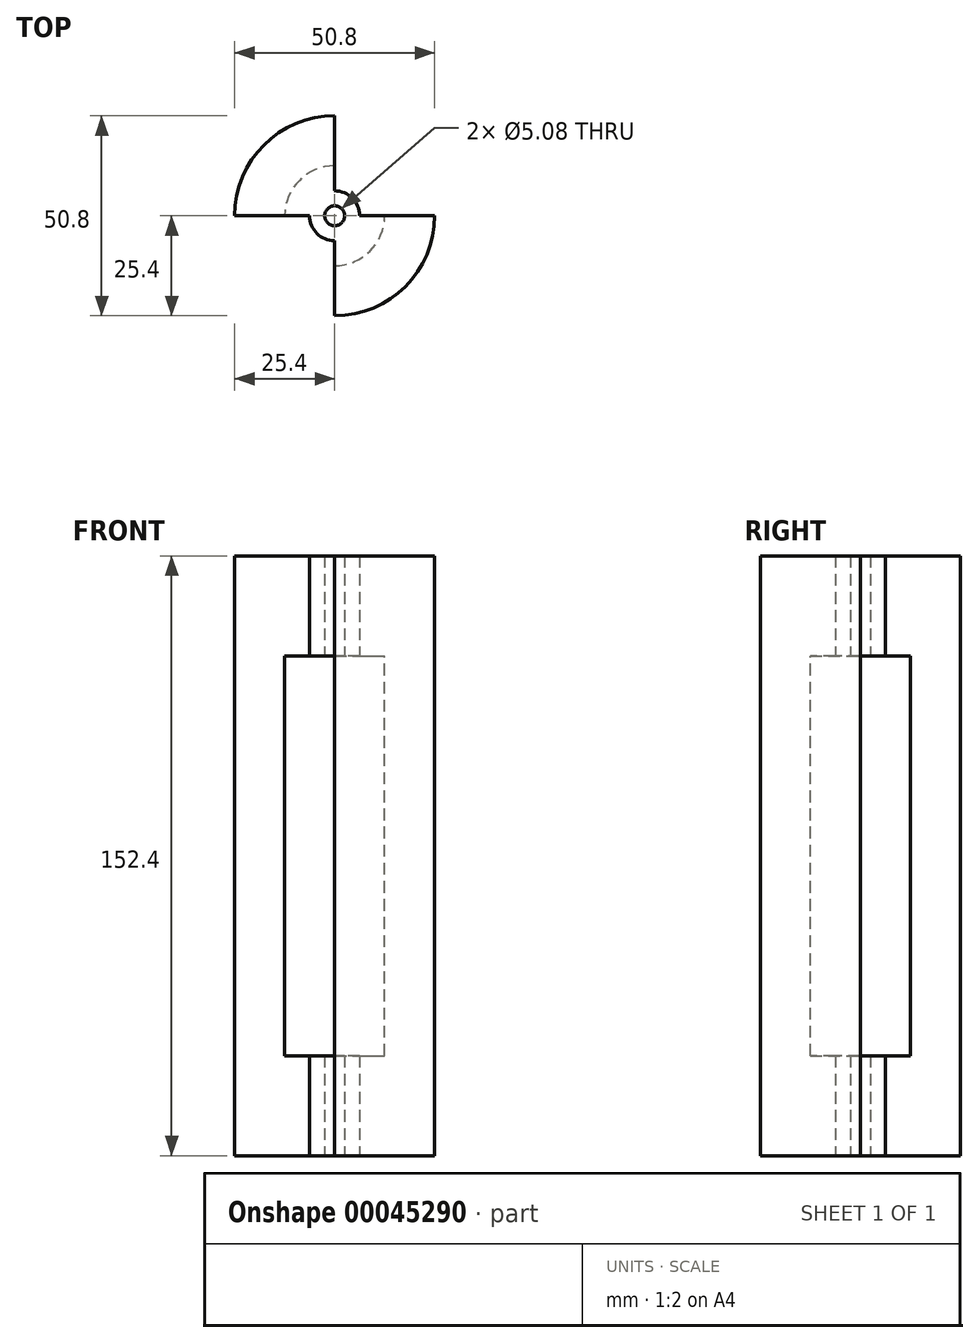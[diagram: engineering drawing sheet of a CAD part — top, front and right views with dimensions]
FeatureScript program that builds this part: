
annotation { "Feature Type Name" : "Feature", "Feature Type Description" : "" }
export const myFeature = defineFeature(function(context is Context, id is Id, definition is map)
    precondition{}
    {
        {
            var Q0;
            Q0=qCreatedBy(makeId("Top.planeOp"),FACE);
            var sketch = newSketch(context, id + "F0", { "sketchPlane" : qUnion([Q0])});
            skArc(sketch, "E0", {"start": v(0, 25.4) * mm, "mid": v(-17.96, 17.96) * mm, "end": v(-25.4, 0) * mm});
            skLineSegment(sketch, "E1", {"start": v(0, 6.35) * mm, "end": v(0, 25.4) * mm});
            skLineSegment(sketch, "E2", {"start": v(0, -6.35) * mm, "end": v(0, -25.4) * mm});
            skLineSegment(sketch, "E3", {"start": v(6.35, 0) * mm, "end": v(25.4, 0) * mm});
            skLineSegment(sketch, "E4", {"start": v(-6.35, 0) * mm, "end": v(-25.4, 0) * mm});
            skArc(sketch, "E5.trimOffspring", {"start": v(0, -25.4) * mm, "mid": v(17.96, -17.96) * mm, "end": v(25.4, 0) * mm});
            skArc(sketch, "E6", {"start": v(-6.35, 0) * mm, "mid": v(-4.5, -4.5) * mm, "end": v(0, -6.35) * mm});
            skArc(sketch, "E7.trimOffspring", {"start": v(6.35, 0) * mm, "mid": v(4.5, 4.5) * mm, "end": v(0, 6.35) * mm});
            skCircle(sketch, "E8", {"center": v(0, 0) * mm, "radius": 2.54 * mm});
            skSolve(sketch);
        }
        {
            var Q0;
            Q0=qSketchRegion(id+"F0",true);
            extrude(context, id + "F1", {"entities" : qUnion([Q0]), "endBound" : BoundingType.SYMMETRIC, "depth" : 152.4 * mm});
        }
        {
            var Q0;
            Q0=makeQuery(id+"F1.opExtrude","CAP_FACE",FACE,{"disambiguationData":[OSD([sQuery(id+"F0.wireOp",EDGE,"E0")])],"isStart":false});
            var sketch = newSketch(context, id + "F2", { "sketchPlane" : qUnion([Q0])});
            skLineSegment(sketch, "E9.left", {"start": v(-6.35, 38.1) * mm, "end": v(-6.35, -38.1) * mm});
            skLineSegment(sketch, "E9.right", {"start": v(6.35, 38.1) * mm, "end": v(6.35, -38.21) * mm});
            skLineSegment(sketch, "E10.1.0.3", {"start": v(31.75, 38.1) * mm, "end": v(31.75, -38.21) * mm});
            skLineSegment(sketch, "E11.1.0.0", {"start": v(-31.75, 38.1) * mm, "end": v(-31.75, -38.1) * mm});
            skPoint(sketch, "E12.orphan", {"position": v(19.05, -38.1) * mm});
            skLineSegment(sketch, "E13", {"start": v(-31.75, 38.1) * mm, "end": v(-6.35, 38.1) * mm});
            skLineSegment(sketch, "E14", {"start": v(6.35, 38.1) * mm, "end": v(31.75, 38.1) * mm});
            skLineSegment(sketch, "E15", {"start": v(31.75, -38.21) * mm, "end": v(6.35, -38.21) * mm});
            skLineSegment(sketch, "E16", {"start": v(-6.35, -38.1) * mm, "end": v(-31.75, -38.1) * mm});
            skSolve(sketch);
        }
        {
            var Q0;
            Q0=qCreatedBy(makeId("Top.planeOp"),FACE);
            var sketch = newSketch(context, id + "F3", { "sketchPlane" : qUnion([Q0])});
            skCircle(sketch, "E17", {"center": v(0, 0) * mm, "radius": 12.7 * mm});
            skSolve(sketch);
        }
        {
            var Q0;
            Q0 = qSketchRegion(id + "F3", true);
            extrude(context, id + "F4", {"entities" : qUnion([Q0]), "operationType" : NewBodyOperationType.REMOVE, "endBound" : BoundingType.SYMMETRIC, "oppositeDirection" : true, "depth" : 101.6 * mm});
        }
    });
